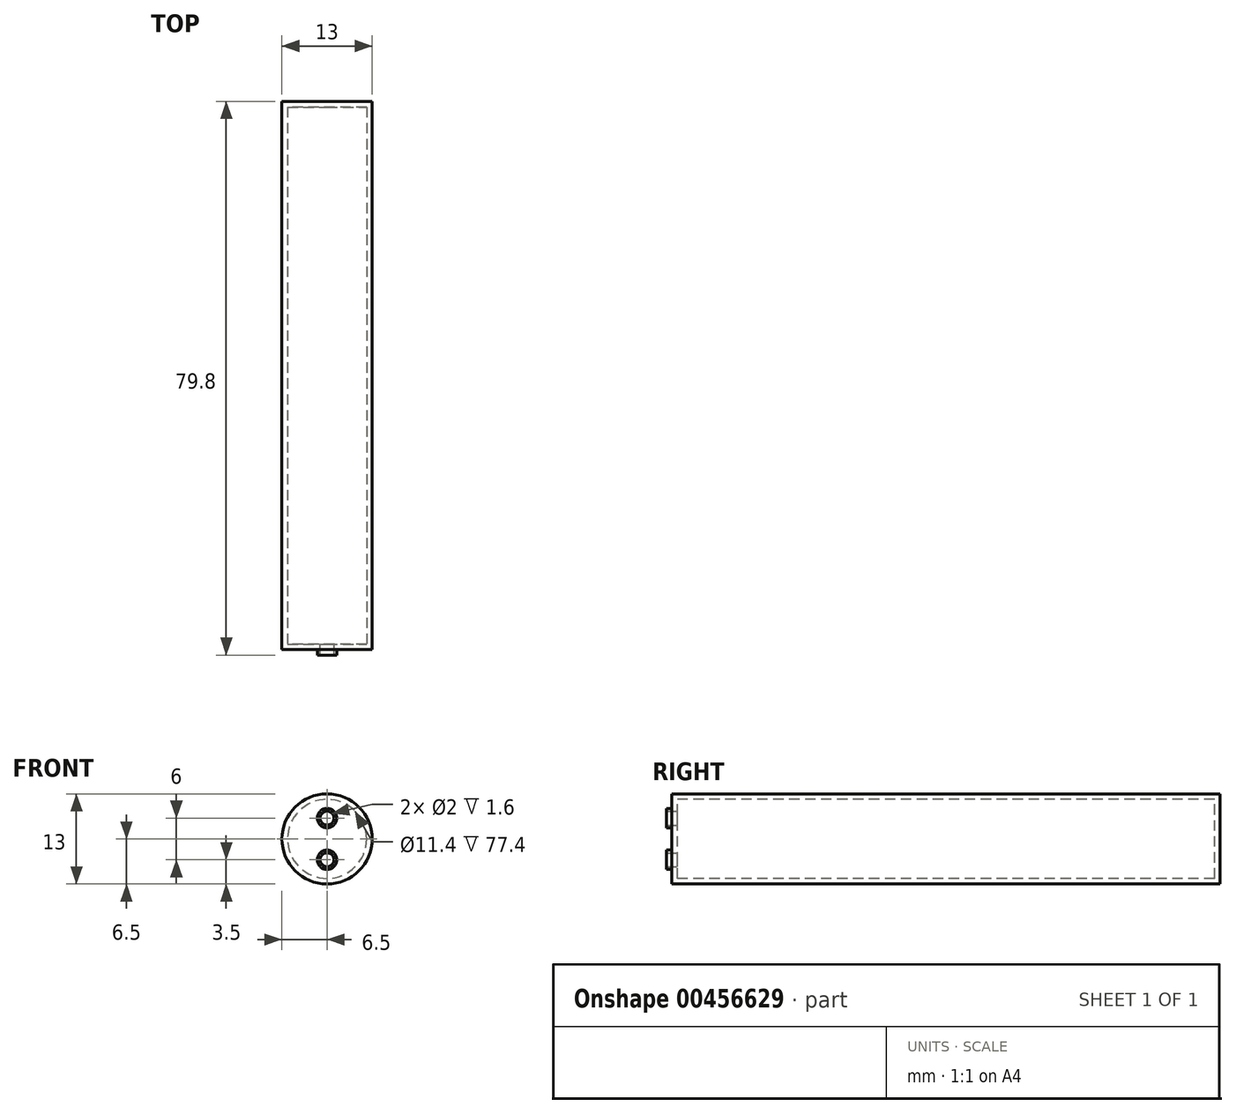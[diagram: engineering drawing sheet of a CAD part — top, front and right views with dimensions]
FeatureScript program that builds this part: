
annotation { "Feature Type Name" : "Feature", "Feature Type Description" : "" }
export const myFeature = defineFeature(function(context is Context, id is Id, definition is map)
    precondition{}
    {
        {
            var Q0;
            Q0=qCreatedBy(makeId("Front.planeOp"),FACE);
            var sketch = newSketch(context, id + "F0", { "sketchPlane" : qUnion([Q0])});
            skCircle(sketch, "E0", {"center": v(6.5, 6.5) * mm, "radius": 6.5 * mm});
            skCircle(sketch, "E1", {"center": v(6.5, 9.5) * mm, "radius": 1.4 * mm});
            skCircle(sketch, "E2", {"center": v(6.5, 3.5) * mm, "radius": 1.4 * mm});
            skLineSegment(sketch, "E3", {"start": v(6.5, 9.5) * mm, "end": v(6.5, 3.5) * mm});
            skCircle(sketch, "E4", {"center": v(6.5, 3.5) * mm, "radius": 1 * mm});
            skCircle(sketch, "E5", {"center": v(6.5, 9.5) * mm, "radius": 1 * mm});
            skSolve(sketch);
        }
        {
            var Q0;
            Q0=makeQuery(id+"F0.imprint","IMPRINT",FACE,{"disambiguationData":[TD([[makeQuery(id+"F0.imprint","IMPRINT",EDGE,{"derivedFrom":sQuery(id+"F0.wireOp",EDGE,"E5")}),1.0]])]});
            var Q1;
            Q1=makeQuery(id+"F0.imprint","IMPRINT",FACE,{"disambiguationData":[TD([[makeQuery(id+"F0.imprint","IMPRINT",EDGE,{"derivedFrom":sQuery(id+"F0.wireOp",EDGE,"E1")}),1.0]])]});
            var Q2;
            Q2=makeQuery(id+"F0.imprint","IMPRINT",FACE,{"disambiguationData":[TD([[makeQuery(id+"F0.imprint","IMPRINT",EDGE,{"derivedFrom":sQuery(id+"F0.wireOp",EDGE,"E0")}),1.0]])]});
            var Q3;
            Q3=makeQuery(id+"F0.imprint","IMPRINT",FACE,{"disambiguationData":[TD([[makeQuery(id+"F0.imprint","IMPRINT",EDGE,{"derivedFrom":sQuery(id+"F0.wireOp",EDGE,"E4")}),1.0]])]});
            var Q4;
            Q4=makeQuery(id+"F0.imprint","IMPRINT",FACE,{"disambiguationData":[TD([[makeQuery(id+"F0.imprint","IMPRINT",EDGE,{"derivedFrom":sQuery(id+"F0.wireOp",EDGE,"E2")}),1.0]])]});
            extrude(context, id + "F1", {"entities" : qUnion([Q0, Q1, Q2, Q3, Q4]), "oppositeDirection" : true, "depth" : 79 * mm});
        }
        {
            var Q0;
            Q0=makeQuery(id+"F1.opExtrude","CAP_FACE",FACE,{"disambiguationData":[OSD([sQuery(id+"F0.wireOp",EDGE,"E0")])],"isStart":true});
            var Q1;
            Q1=makeQuery(id+"F1.opExtrude","SWEPT_BODY",BODY,{"disambiguationData":[OSD([sQuery(id+"F0.wireOp",EDGE,"E0")])]});
            shell(context, id + "F2", {"entities" : qUnion([Q0]), "parts" : qUnion([Q1]), "thickness" : .8 * mm});
        }
        {
            var Q0;
            Q0=makeQuery(id+"F0.imprint","IMPRINT",FACE,{"disambiguationData":[TD([[makeQuery(id+"F0.imprint","IMPRINT",EDGE,{"derivedFrom":sQuery(id+"F0.wireOp",EDGE,"E0")}),1.0]])]});
            extrude(context, id + "F3", {"entities" : qUnion([Q0]), "operationType" : NewBodyOperationType.ADD, "oppositeDirection" : true, "depth" : .8 * mm});
        }
        {
            var Q0;
            Q0=makeQuery(id+"F0.imprint","IMPRINT",FACE,{"disambiguationData":[TD([[makeQuery(id+"F0.imprint","IMPRINT",EDGE,{"derivedFrom":sQuery(id+"F0.wireOp",EDGE,"E1")}),1.0]])]});
            var Q1;
            Q1=makeQuery(id+"F0.imprint","IMPRINT",FACE,{"disambiguationData":[TD([[makeQuery(id+"F0.imprint","IMPRINT",EDGE,{"derivedFrom":sQuery(id+"F0.wireOp",EDGE,"E2")}),1.0]])]});
            extrude(context, id + "F4", {"entities" : qUnion([Q0, Q1]), "operationType" : NewBodyOperationType.ADD, "endBound" : BoundingType.SYMMETRIC, "depth" : 1.6 * mm});
        }
    });
